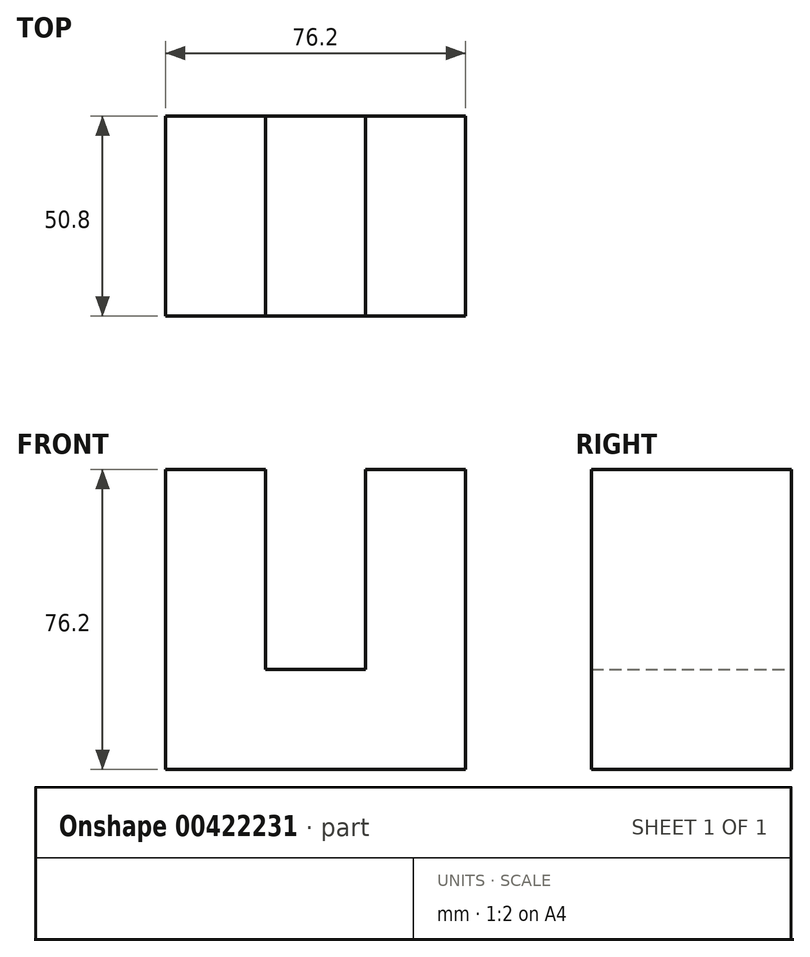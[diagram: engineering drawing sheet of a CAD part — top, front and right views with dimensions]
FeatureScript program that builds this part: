
annotation { "Feature Type Name" : "Feature", "Feature Type Description" : "" }
export const myFeature = defineFeature(function(context is Context, id is Id, definition is map)
    precondition{}
    {
        {
            var Q0;
            Q0=qCreatedBy(makeId("Front.planeOp"),FACE);
            var sketch = newSketch(context, id + "F0", { "sketchPlane" : qUnion([Q0])});
            skLineSegment(sketch, "E0", {"start": v(-50.8, 70.67) * mm, "end": v(-50.8, -5.53) * mm});
            skLineSegment(sketch, "E1", {"start": v(-50.8, 70.67) * mm, "end": v(-25.4, 70.67) * mm});
            skLineSegment(sketch, "E2", {"start": v(-25.4, 70.67) * mm, "end": v(-25.4, 19.87) * mm});
            skLineSegment(sketch, "E3", {"start": v(-25.4, 19.87) * mm, "end": v(0, 19.87) * mm});
            skLineSegment(sketch, "E4", {"start": v(0, 19.87) * mm, "end": v(0, 70.67) * mm});
            skLineSegment(sketch, "E5", {"start": v(0, 70.67) * mm, "end": v(25.4, 70.67) * mm});
            skLineSegment(sketch, "E6", {"start": v(25.4, 70.67) * mm, "end": v(25.4, -5.53) * mm});
            skLineSegment(sketch, "E7", {"start": v(-50.8, -5.53) * mm, "end": v(25.4, -5.53) * mm});
            skSolve(sketch);
        }
        {
            var Q0;
            Q0 = qSketchRegion(id + "F0", true);
            extrude(context, id + "F1", {"entities" : qUnion([Q0]), "depth" : 50.8 * mm});
        }
    });
